# Revit family: Seating_Inc-Seat_Connectable_Bariatric-Cobra
name_source: partatom
category: Furniture
revit_build: Autodesk Revit 2014 (Build: 20130308_1515(x64)
units: mm (PartAtom-declared; Revit-internal decimal feet)

## types (30) — shared parameters
# Leg = 3
# Seat = 2
Arm Plastic Finish = STI - Plastic Black
Assembly Code = E2020200
Back Finish = STI - Upholstery Latex
Depth = 25 1/2"
Glide Finish = STI - Plastic Black
Height = 34"
Keynote = 12500
Low Emitting Finish = Yes
Low Emitting Material = Yes
Manufacturer = Seating Inc
Salvage or Reuse = Yes
Seat Finish = STI - Upholstery Latex
Type Comments = Cobra Tandem Seating
URL = www.seatinginc.com
zero-valued in all types: Percentage of Recycled Content

## per-type parameters (varying)
| type | # Arm | Arm | Arm Dist | Arm Metal Finish | Description | Leg Finish | Origin Arm | Seat | Support Finish | Width |
| CM763-43B | 2 | No | 43 3/4" | STI - Power Coat, Black | Black Armless | STI - Power Coat, Black | 1 1/4" | 23" | STI - Power Coat, Black | 45" |
| CM763-43S | 2 | No | 43 3/4" | STI - Power Coat, Silver | Silver Armless | STI - Power Coat, Silver | 1 1/4" | 23" | STI - Power Coat, Silver | 45" |
| CM764-43B | 2 | Yes | 43 3/4" | STI - Power Coat, Black | Black w/Arms | STI - Power Coat, Black | 1 1/4" | 23" | STI - Power Coat, Black | 45" |
| CM764-43S | 2 | Yes | 43 3/4" | STI - Power Coat, Silver | Silver w/Arms | STI - Power Coat, Silver | 1 1/4" | 23" | STI - Power Coat, Silver | 45" |
| CM765-43B | 2 | Yes | 0" | STI - Power Coat, Black | Black, Left Arm | STI - Power Coat, Black | 1 1/4" | 23" | STI - Power Coat, Black | 45" |
| CM765-43S | 2 | Yes | 0" | STI - Power Coat, Silver | Silver, Left Arm | STI - Power Coat, Silver | 1 1/4" | 23" | STI - Power Coat, Silver | 45" |
| CM766-43B | 2 | Yes | 0" | STI - Power Coat, Black | Black, Right Arm | STI - Power Coat, Black | 45" | 23" | STI - Power Coat, Black | 45" |
| CM766-43S | 2 | Yes | 0" | STI - Power Coat, Silver | Silver, Right Arm | STI - Power Coat, Silver | 45" | 23" | STI - Power Coat, Silver | 45" |
| CM767-43B | 3 | Yes | 43 3/4" | STI - Power Coat, Black | Black, 3 Arms | STI - Power Coat, Black | 1 1/4" | 23" | STI - Power Coat, Black | 45" |
| CM767-43S | 3 | Yes | 43 3/4" | STI - Power Coat, Silver | Silver, 3 Arms | STI - Power Coat, Silver | 1 1/4" | 23" | STI - Power Coat, Silver | 45" |
| CM763-49B | 2 | No | 49 3/4" | STI - Power Coat, Black | Black Armless | STI - Power Coat, Black | 1 1/4" | 26" | STI - Power Coat, Black | 51" |
| CM763-49S | 2 | No | 49 3/4" | STI - Power Coat, Silver | Silver Armless | STI - Power Coat, Silver | 1 1/4" | 26" | STI - Power Coat, Silver | 51" |
| CM764-49B | 2 | Yes | 49 3/4" | STI - Power Coat, Black | Black w/Arms | STI - Power Coat, Black | 1 1/4" | 26" | STI - Power Coat, Black | 51" |
| CM764-49S | 2 | Yes | 49 3/4" | STI - Power Coat, Silver | Silver w/Arms | STI - Power Coat, Silver | 1 1/4" | 26" | STI - Power Coat, Silver | 51" |
| CM765-49B | 2 | Yes | 0" | STI - Power Coat, Black | Black, Left Arm | STI - Power Coat, Black | 1 1/4" | 26" | STI - Power Coat, Black | 51" |
| CM765-49S | 2 | Yes | 0" | STI - Power Coat, Silver | Silver, Left Arm | STI - Power Coat, Silver | 1 1/4" | 26" | STI - Power Coat, Silver | 51" |
| CM766-49B | 2 | Yes | 0" | STI - Power Coat, Black | Black, Right Arm | STI - Power Coat, Black | 51" | 26" | STI - Power Coat, Black | 51" |
| CM766-49S | 2 | Yes | 0" | STI - Power Coat, Silver | Silver, Right Arm | STI - Power Coat, Silver | 51" | 26" | STI - Power Coat, Silver | 51" |
| CM767-49B | 3 | Yes | 49 3/4" | STI - Power Coat, Black | Black, 3 Arms | STI - Power Coat, Black | 1 1/4" | 26" | STI - Power Coat, Black | 51" |
| CM767-49S | 3 | Yes | 49 3/4" | STI - Power Coat, Silver | Silver, 3 Arms | STI - Power Coat, Silver | 1 1/4" | 26" | STI - Power Coat, Silver | 51" |
| CM763-61B | 2 | No | 61 3/4" | STI - Power Coat, Black | Black Armless | STI - Power Coat, Black | 1 1/4" | 32" | STI - Power Coat, Black | 63" |
| CM763-61S | 2 | No | 61 3/4" | STI - Power Coat, Silver | Silver Armless | STI - Power Coat, Silver | 1 1/4" | 32" | STI - Power Coat, Silver | 63" |
| CM764-61B | 2 | Yes | 61 3/4" | STI - Power Coat, Black | Black w/Arms | STI - Power Coat, Black | 1 1/4" | 32" | STI - Power Coat, Black | 63" |
| CM764-61S | 2 | Yes | 61 3/4" | STI - Power Coat, Silver | Silver w/Arms | STI - Power Coat, Silver | 1 1/4" | 32" | STI - Power Coat, Silver | 63" |
| CM765-61B | 2 | Yes | 0" | STI - Power Coat, Black | Black, Left Arm | STI - Power Coat, Black | 1 1/4" | 32" | STI - Power Coat, Black | 63" |
| CM765-61S | 2 | Yes | 0" | STI - Power Coat, Silver | Silver, Left Arm | STI - Power Coat, Silver | 1 1/4" | 32" | STI - Power Coat, Silver | 63" |
| CM766-61B | 2 | Yes | 0" | STI - Power Coat, Black | Black, Right Arm | STI - Power Coat, Black | 63" | 32" | STI - Power Coat, Black | 63" |
| CM766-61S | 2 | Yes | 0" | STI - Power Coat, Silver | Silver, Right Arm | STI - Power Coat, Silver | 63" | 32" | STI - Power Coat, Silver | 63" |
| CM767-61B | 3 | Yes | 61 3/4" | STI - Power Coat, Black | Black, 3 Arms | STI - Power Coat, Black | 1 1/4" | 32" | STI - Power Coat, Black | 63" |
| CM767-61S | 3 | Yes | 61 3/4" | STI - Power Coat, Silver | Silver, 3 Arms | STI - Power Coat, Silver | 1 1/4" | 32" | STI - Power Coat, Silver | 63" |

note: column(s) folded — value = type name in every type: Model

## geometry (parser evidence)
native form markers: Sweep x13
no freeform markers — native parametric forms only
